# Revit family: EURS_63_LF_FB_CoreLine Surface Mounted SM136V 20x150
name_source: partatom
category: Lighting Fixtures
revit_build: Autodesk Revit 2018 (Build: 20190510_1515(x64)
units: mm (PartAtom-declared; Revit-internal decimal feet)

## family parameters
Cut with Voids When Loaded = No
Host = Face
Light Source = No
Part Type = Normal
Room Calculation Point = No
Round Connector Dimension = Use Diameter
Shared = Yes

## types (1)
- Type catalog
    12NC = 12NC CODE
    Apparent Load = 0 VA
    BIM Library - URL = http://www.lighting.philips.com
    Content modified date = DATE
    Content version = 1.0
    Default Elevation = 0 mm  [stored 0 ft]
    Description = CoreLine
    EOC = EOC CODE
    ETIM code = EC002892
    ETIM code URL = https://prod.etim-international.com
    Fixture code = FIXTURE CODE
    Height = 59 mm
    Height 01 = 10 mm  [stored 0.0328084 ft]
    Lamp = LAMP TYPE
    Last IES update = DATE
    Length = 1430 mm  [stored 4.6916 ft]
    Length 01 = 1345 mm
    Light source = 2 mm  [stored 0.00656168 ft]
    Manufacturer = Philips
    Model = SM136V 20x150
    Order code = ORDER CODE
    Product catalog - URL = MODEL WEBPAGE
    Thickness 01 = 30 mm  [stored 0.0984252 ft]
    Type Comments = Face Based
    URL = http://www.lighting.philips.com
    Voltage (V) = 230 V
    Width = 200 mm  [stored 0.656168 ft]
    Width 01 = 105 mm  [stored 0.344488 ft]

note: [stored X ft] marks values corroborated as IEEE doubles in the binary element streams (Revit-internal decimal feet)

## geometry (parser evidence)
native form markers: Sweep x6
no freeform markers — native parametric forms only
